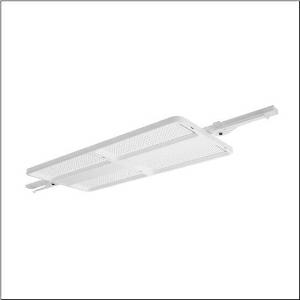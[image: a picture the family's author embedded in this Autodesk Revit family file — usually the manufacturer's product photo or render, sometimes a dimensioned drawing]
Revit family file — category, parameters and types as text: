
# Revit family: highbay_11_fur_modario_r__tragschiene_maxi_51hn11db6tma_13df
name_source: partatom
category: Lighting Fixtures
units: mm (PartAtom-declared; Revit-internal decimal feet)

## family parameters
Cut with Voids When Loaded = No
Host = Face
Light Source = No
Part Type = Normal
Room Calculation Point = No
Round Connector Dimension = Use Diameter
Shared = No

## types (1)
- --- (1 x LED, 53100 lm, 295.1 W, 6500K)
    Apparent Load = 295 VA
    CIE Flux Codes = 85 97 100 100 100
    Color Rendering = 80
    Color Temperature = 6500K
    Default Elevation = 1800 mm
    Description = high bay luminaire Highbay 11 for Modario® trunking rail maxi; direct symmetric narrow distribution, light control with lens of PMMA; UGR ≤ 22 (X = 4H | Y = 8H | S = 0.25H | reflection values 70/50/20); luminous flux: 53.100lm; light colour: 865, colour temperature: 6500K, MacAdam ≤ 2 SDCM (initial), colour rendering: CRI > 80; luminous efficacy: 179,9lm/W; rated service life: 100.000h (L95/B50) at AT= 25°C; control: DALI 2; luminaire connection: plug, 5-pole, with phase selectionmains connection: 230..240V, AC 50/60Hz; connected load: 295,1W; protection rating (complete): IP64; insulation class (complete): insulation class I (protective earthing); protection symbol: D; impact resistance: IK07; certification: CE, ENEC, VDE, UKCA; internal wiring halogen-free; luminaire corresponds to IFS (International Featured Standards) requirements for safety and quality in the food industry; LABS conformity tested according to VDMA 24364:2018-05; housing frame of high-performance plastic PA6, matt traffic white (RAL 9016); cover of PMMA; fixing on rail side of steel, galvanised, white; blank cover of PC, traffic white (RAL 9016); dimension (LxWxH): 1.496 x 442 x 72mm; permissible operating ambient temperature: -40..+50°C (reducing of maximum allowable ambient temperature of 5°C with ceiling mounting); packaging unit: 1 piece
    Height = 72 mm  [stored 0.23622 ft]
    Lamp = 1 x LED
    Lamp Light Flux = 53100 lm
    Lamp Power = 295.1 W
    Lamp count = 1
    Length = 946 mm
    Luminous efficacy = 180 lm/W
    Manufacturer = Siteco
    ModVariant = No
    Model = 51HN11DB6TMA
    Mounting Place = Ceiling
    Mounting Type = Pendant
    Number of Poles = 1
    OnlyDefault = Yes
    Power Factor = 1
    Product Name = Highbay 11 für Modario® Tragschiene maxi
    Product group = high bay luminaire
    ProductGroupID = 901
    Protection Class = Protection class I
    Protection Degree = IP 64
    RLX_Detail_Level = 1
    RLX_Emergency_Light_Flux = 0 lm
    RLX_Emergency_Type = 0
    RLX_Emergency_Type_DB = No
    RlxData = <blob elided: 21453 chars, md5=9ad7de23>
    Socket = socket
    Standby Power = 0 W
    System Light Flux = 53100 lm
    System Power = 295 W
    Type Comments = factory setting: luminous flux: 100 % | dim-lin: 254 | 664 mA
    Type Image = l_1363248.jpg
    URL = http://relux.com
    VarID = @adj_004393
    Voltage = 0 V
    Weight = 0.00 kg
    Width = 442 mm

note: [stored X ft] marks values corroborated as IEEE doubles in the binary element streams (Revit-internal decimal feet)

## geometry (parser evidence)
native form markers: Blend x4, Sweep x12
no freeform markers — native parametric forms only
